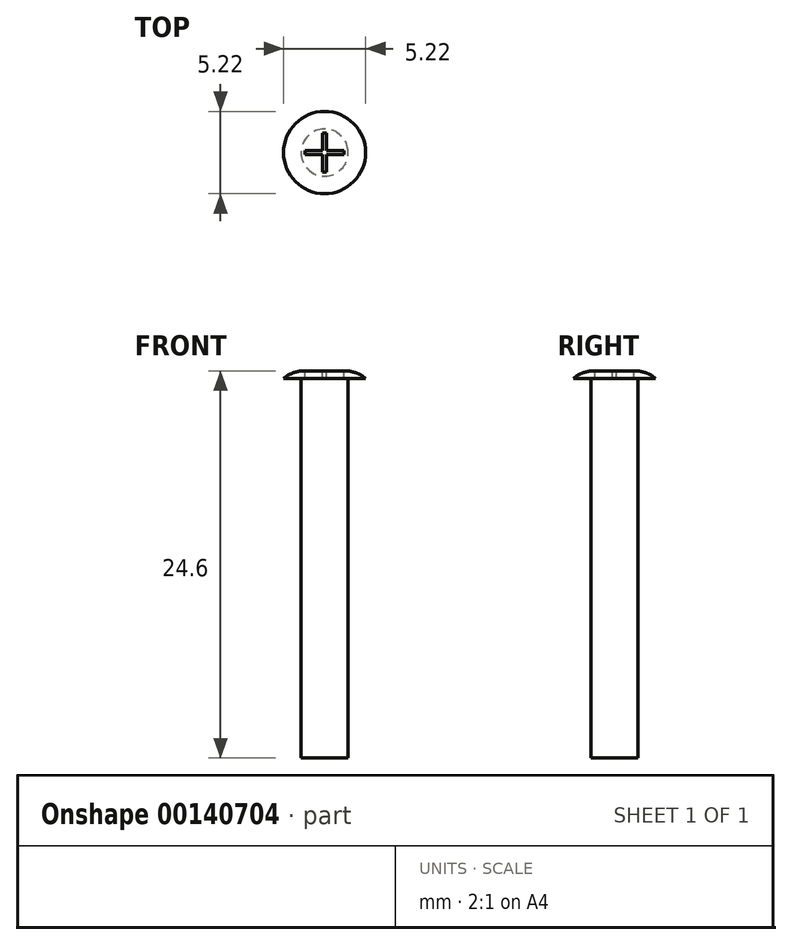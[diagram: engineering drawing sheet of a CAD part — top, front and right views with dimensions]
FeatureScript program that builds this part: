
annotation { "Feature Type Name" : "Feature", "Feature Type Description" : "" }
export const myFeature = defineFeature(function(context is Context, id is Id, definition is map)
    precondition{}
    {
        {
            var Q0;
            Q0=qCreatedBy(makeId("Top.planeOp"),FACE);
            var sketch = newSketch(context, id + "F0", { "sketchPlane" : qUnion([Q0])});
            skCircle(sketch, "E0", {"center": v(0, 0) * mm, "radius": 1.5 * mm});
            skSolve(sketch);
        }
        {
            var Q0;
            Q0=makeQuery(id+"F0.imprint","IMPRINT",FACE,{"disambiguationData":[TD([[makeQuery(id+"F0.imprint","IMPRINT",EDGE,{"derivedFrom":sQuery(id+"F0.wireOp",EDGE,"E0")}),1.0]])]});
            extrude(context, id + "F1", {"entities" : qUnion([Q0]), "depth" : 24.6 * mm});
        }
        {
            var Q0;
            Q0=makeQuery(id+"F1.opExtrude","CAP_FACE",FACE,{"disambiguationData":[OSD([sQuery(id+"F0.wireOp",EDGE,"E0")])],"isStart":false});
            var sketch = newSketch(context, id + "F2", { "sketchPlane" : qUnion([Q0])});
            skCircle(sketch, "E1.0", {"center": v(0, 0) * mm, "radius": 1.5 * mm});
            skCircle(sketch, "E2", {"center": v(0, 0) * mm, "radius": 2.6 * mm});
            skLineSegment(sketch, "E3", {"start": v(-1.25, -0.12) * mm, "end": v(-0.12, -0.12) * mm});
            skLineSegment(sketch, "E4", {"start": v(-1.25, 0.12) * mm, "end": v(-0.12, 0.12) * mm});
            skLineSegment(sketch, "E5", {"start": v(-0.12, -1.25) * mm, "end": v(-0.12, -0.12) * mm});
            skLineSegment(sketch, "E6", {"start": v(0.12, -1.25) * mm, "end": v(0.12, -0.12) * mm});
            skLineSegment(sketch, "E7.trimOffspring", {"start": v(-0.12, 0.12) * mm, "end": v(-0.12, 1.25) * mm});
            skLineSegment(sketch, "E8.trimOffspring", {"start": v(0.12, -0.12) * mm, "end": v(1.25, -0.12) * mm});
            skLineSegment(sketch, "E9.trimOffspring", {"start": v(0.12, 0.12) * mm, "end": v(1.25, 0.12) * mm});
            skLineSegment(sketch, "E10.trimOffspring", {"start": v(0.12, 0.12) * mm, "end": v(0.12, 1.25) * mm});
            skLineSegment(sketch, "E11", {"start": v(-1.25, -0.12) * mm, "end": v(-1.25, 0.12) * mm});
            skLineSegment(sketch, "E12", {"start": v(-0.12, -1.25) * mm, "end": v(0.12, -1.25) * mm});
            skLineSegment(sketch, "E13", {"start": v(1.25, -0.12) * mm, "end": v(1.25, 0.12) * mm});
            skLineSegment(sketch, "E14", {"start": v(-0.12, 1.25) * mm, "end": v(0.12, 1.25) * mm});
            skSolve(sketch);
        }
        {
            var Q0;
            Q0 = qSketchRegion(id + "F2", true);
            extrude(context, id + "F3", {"entities" : qUnion([Q0]), "operationType" : NewBodyOperationType.ADD, "oppositeDirection" : true, "depth" : 0.5 * mm});
        }
        {
            var Q0;
            Q0=makeQuery(id+"F3.opExtrude","CAP_EDGE",EDGE,{"disambiguationData":[OSD([sQuery(id+"F2.wireOp",EDGE,"E2")])],"isStart":true});
            fillet(context, id + "F4", {"entities" : qUnion([Q0]), "radius" : 2 * mm, "tangentPropagation" : true, "allowEdgeOverflow" : false});
        }
        {
            var Q0;
            Q0=makeQuery(id+"F2.imprint","IMPRINT",FACE,{"disambiguationData":[TD([[makeQuery(id+"F2.imprint","IMPRINT",EDGE,{"derivedFrom":sQuery(id+"F2.wireOp",EDGE,"E3")}),1.0]])]});
            extrude(context, id + "F5", {"entities" : qUnion([Q0]), "operationType" : NewBodyOperationType.REMOVE, "oppositeDirection" : true, "depth" : 0.5 * mm});
        }
    });
